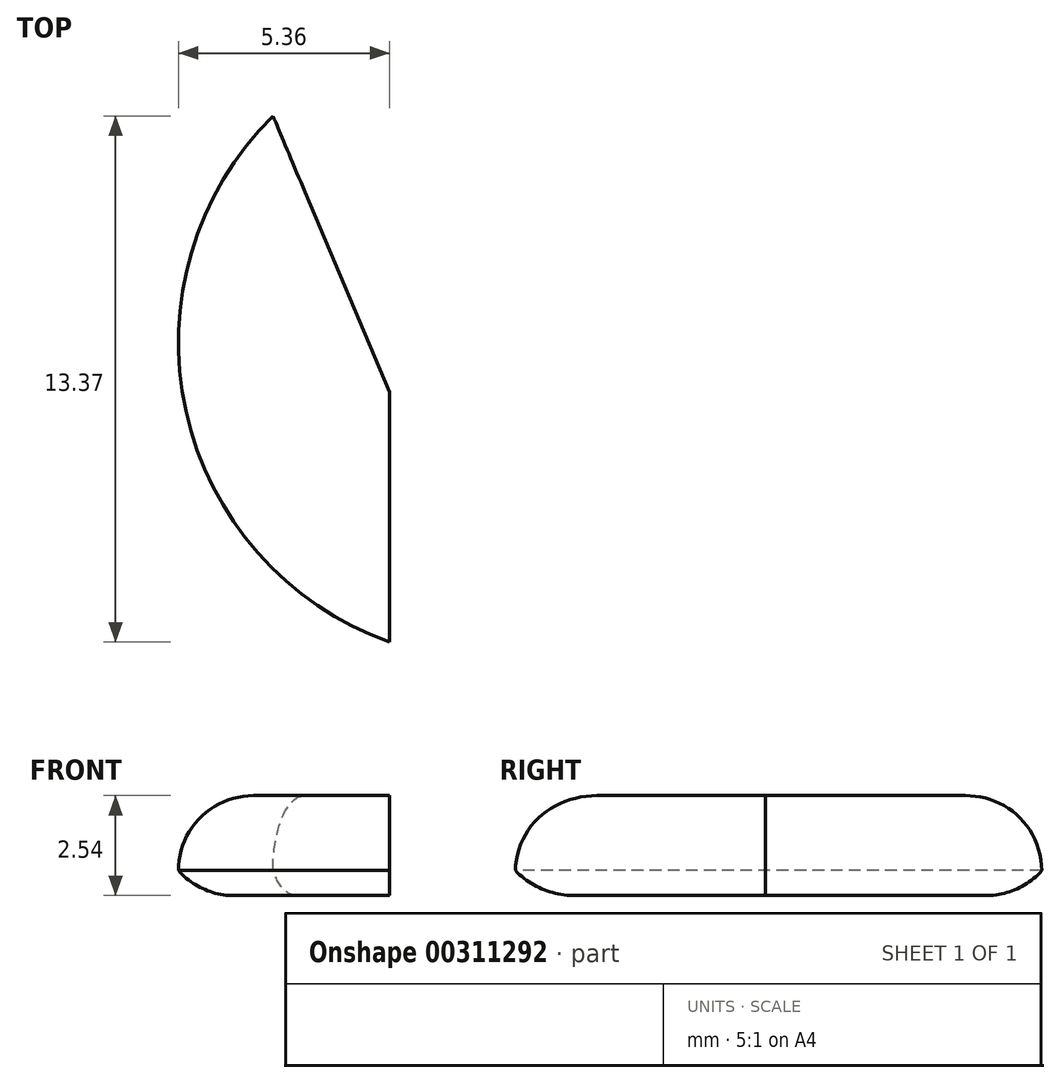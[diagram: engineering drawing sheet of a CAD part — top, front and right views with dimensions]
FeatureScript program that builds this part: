
annotation { "Feature Type Name" : "Feature", "Feature Type Description" : "" }
export const myFeature = defineFeature(function(context is Context, id is Id, definition is map)
    precondition{}
    {
        {
            var Q0;
            Q0=qCreatedBy(makeId("Top.planeOp"),FACE);
            var sketch = newSketch(context, id + "F0", { "sketchPlane" : qUnion([Q0])});
            skLineSegment(sketch, "E0", {"start": v(0, 0) * mm, "end": v(-2.96, 7.02) * mm});
            skLineSegment(sketch, "E1", {"start": v(0, 0) * mm, "end": v(0, -6.35) * mm});
            skArc(sketch, "E2", {"start": v(-2.96, 7.02) * mm, "mid": v(-5.17, -0.48) * mm, "end": v(0, -6.35) * mm});
            skSolve(sketch);
        }
        {
            var Q0;
            Q0=makeQuery(id+"F0.imprint","IMPRINT",FACE,{"disambiguationData":[TD([[makeQuery(id+"F0.imprint","IMPRINT",EDGE,{"derivedFrom":sQuery(id+"F0.wireOp",EDGE,"E0")}),1.0]])]});
            extrude(context, id + "F1", {"entities" : qUnion([Q0]), "depth" : 2.54 * mm});
        }
        {
            var Q0;
            Q0=makeQuery(id+"F1.opExtrude","CAP_EDGE",EDGE,{"disambiguationData":[OSD([sQuery(id+"F0.wireOp",EDGE,"E2")])],"isStart":false});
            fillet(context, id + "F2", {"entities" : qUnion([Q0]), "radius" : 1.9 * mm, "tangentPropagation" : true, "allowEdgeOverflow" : false});
        }
        {
            var Q0;
            Q0=makeQuery(id+"F1.opExtrude","CAP_EDGE",EDGE,{"disambiguationData":[OSD([sQuery(id+"F0.wireOp",EDGE,"E2")])],"isStart":true});
            fillet(context, id + "F3", {"entities" : qUnion([Q0]), "radius" : 1.9 * mm, "tangentPropagation" : true, "allowEdgeOverflow" : false});
        }
    });
